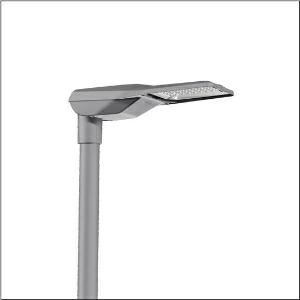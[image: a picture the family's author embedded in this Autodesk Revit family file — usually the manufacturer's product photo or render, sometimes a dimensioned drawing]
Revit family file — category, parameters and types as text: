
# Revit family: streetlight_sl_21_iq_mini___stw1_0a_5xe2e41d08hb_667c
name_source: partatom
category: Lighting Fixtures
units: mm (PartAtom-declared; Revit-internal decimal feet)

## family parameters
Cut with Voids When Loaded = No
Host = Face
Light Source = No
Part Type = Normal
Room Calculation Point = No
Round Connector Dimension = Use Diameter
Shared = No

## types (1)
- --- (1 x LED, 9860 lm, 70.9 W, 4000K)
    Apparent Load = 71 VA
    CIE Flux Codes = 38 75 98 100 100
    Color Rendering = 70
    Color Temperature = 4000K
    Default Elevation = 1800 mm
    Description = Streetlight SL 21 iQ mini, mast luminaire, primary light control with lens, of PMMA, primary optical cover: cover, of toughened safety glass, transparent, light distribution: STW1.0a, light emission: direct distribution, primary light characteristic: asymmetric, installation type: post-top, side-entry, LED, High Power LED, rated luminous flux: 9.860lm, luminous efficacy: 139lm/W, light colour: 740, colour temperature: 4000K, control: Auto-Match, Temp-Guard, Lumen-Switch, Night-Set, Smart-Wire, Light-Fading, Desk-Remote (wireless, voltage-free reading and setting of iQ features in the workshop via application-optimized NFC function/RFID function), optimised constant luminous flux control (CLO 2.0), presetting dimming linear, mains connection: 220..240V, AC, 50/60Hz, start of lifetime: 71W, end of service life: 75W, reduction: 31W, luminaire housing, of diecast aluminium, powder-coated, Siteco® metallic grey (DB 702S), corrosivity category C5 mid according to DIN EN ISO 12944, please order mast flange separately, inclination adjustable: 0°, 5°, 10°, 15°, sealing non-destructively replaceable, multi-level sealing system, length: 628mm, width: 235mm, height: 110mm, mast flange for spigot size: 42mm (side-entry): 5XC10008XM4, 60/48mm (side-entry/post-top): 5XC10108XM2, 76/60mm (side-entry/post-top): 5XC10108XM1, protection rating (complete): IP66, insulation class (complete): insulation class II (safety insulation), certification: CE, ENEC, ENEC+, VDE, impact resistance: IK09, permissible operating ambient temperature for outdoor applications: -40..+50°C, standard-compliant lighting for roads and squares, packaging unit: 1 piece

Light Distribution: STW1.0a
    Height = 110 mm
    Lamp = 1 x LED
    Lamp Light Flux = 9860 lm
    Lamp Power = 70.9 W
    Lamp count = 1
    Length = 625 mm
    Luminous efficacy = 139 lm/W
    Manufacturer = Siteco
    ModVariant = No
    Model = 5XE2E41D08HB
    Number of Poles = 1
    OnlyDefault = Yes
    Power Factor = 1
    Product Name = Streetlight SL 21 iQ mini | STW1.0a
    Product group = mast luminaire | pylon top
    ProductGroupID = 6100
    Protection Class = Protection class II
    Protection Degree = IP 66
    RLX_Detail_Level = 1
    RLX_Emergency_Light_Flux = 0 lm
    RLX_Emergency_Type = 0
    RLX_Emergency_Type_DB = No
    RlxData = <blob elided: 92489 chars, md5=61af5f7e>
    Socket = socket
    Standby Power = 0 W
    System Light Flux = 9860 lm
    System Power = 71 W
    Type Comments = factory setting: luminous flux: 100 % | dim-lin: 254 | 711 mA
    Type Image = l_1003519.jpg
    URL = http://relux.com
    VarID = @adj_090115
    Voltage = 0 V
    Weight = 0.00 kg
    Width = 234 mm

## geometry (parser evidence)
native form markers: Blend x4, Sweep x10
no freeform markers — native parametric forms only
